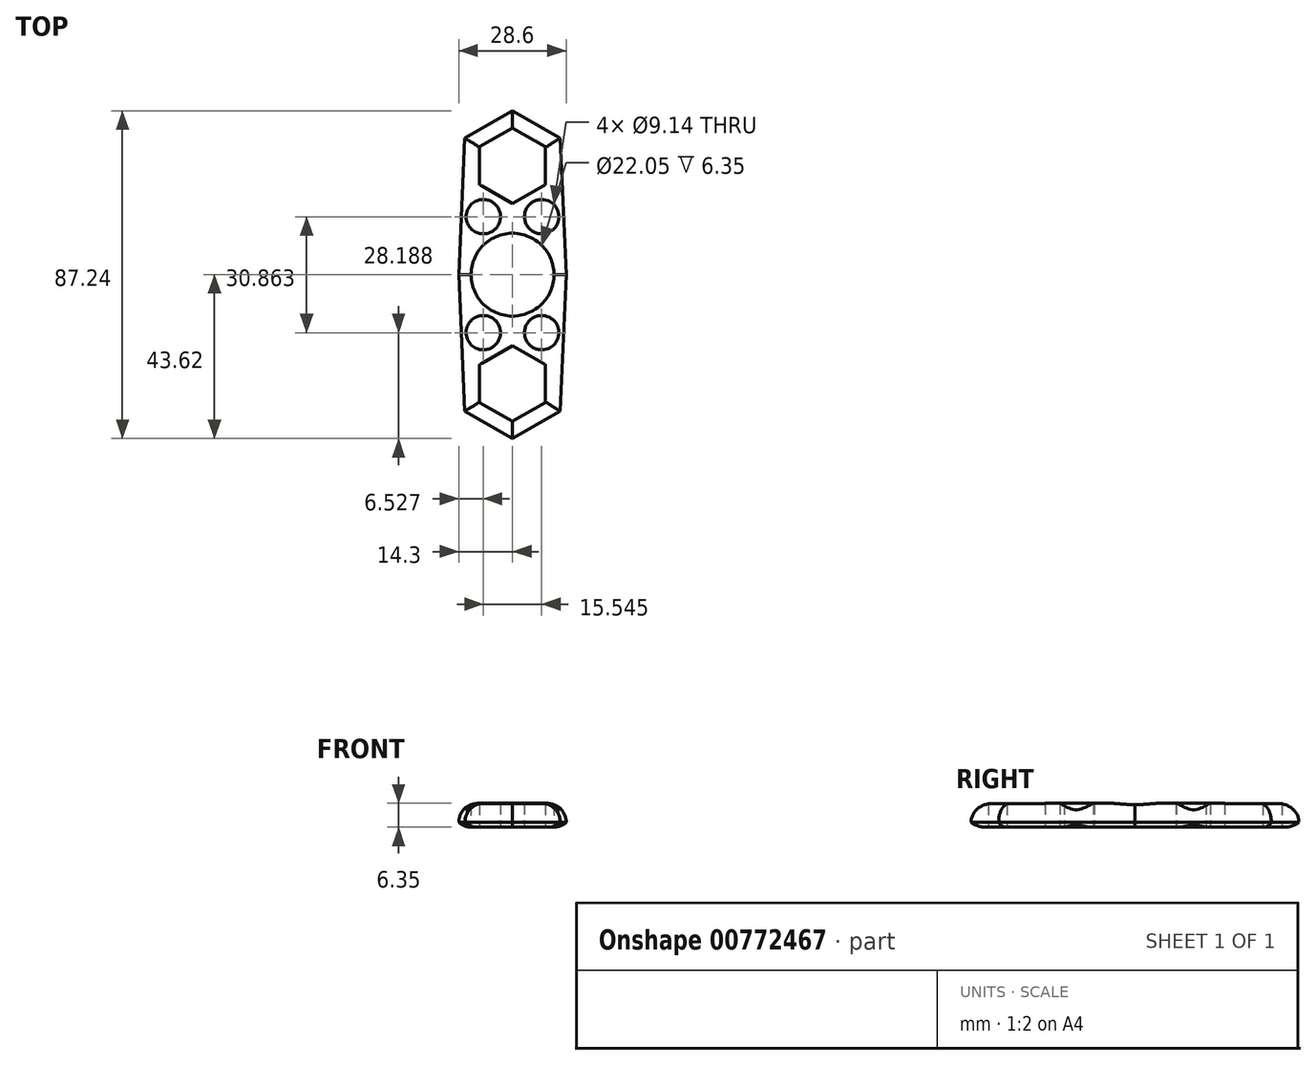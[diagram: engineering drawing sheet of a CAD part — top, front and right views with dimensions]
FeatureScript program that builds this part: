
annotation { "Feature Type Name" : "Feature", "Feature Type Description" : "" }
export const myFeature = defineFeature(function(context is Context, id is Id, definition is map)
    precondition{}
    {
        {
            var Q0;
            Q0=qCreatedBy(makeId("Top.planeOp"),FACE);
            var sketch = newSketch(context, id + "F0", { "sketchPlane" : qUnion([Q0])});
            skCircle(sketch, "E0", {"center": v(0, 0) * mm, "radius": 14.29 * mm});
            skCircle(sketch, "E1", {"center": v(0, 0) * mm, "radius": 11.02 * mm});
            skCircle(sketch, "E2.cCircle", {"center": v(0, 28.95) * mm, "radius": 12.7 * mm, "construction": true});
            skLineSegment(sketch, "E2.0", {"start": v(0, 14.29) * mm, "end": v(-12.7, 21.62) * mm});
            skLineSegment(sketch, "E2.1", {"start": v(-12.7, 21.62) * mm, "end": v(-12.7, 36.28) * mm});
            skLineSegment(sketch, "E2.2", {"start": v(-12.7, 36.28) * mm, "end": v(0, 43.62) * mm});
            skLineSegment(sketch, "E2.3", {"start": v(0, 43.62) * mm, "end": v(12.7, 36.28) * mm});
            skLineSegment(sketch, "E2.4", {"start": v(12.7, 36.28) * mm, "end": v(12.7, 21.62) * mm});
            skLineSegment(sketch, "E2.5", {"start": v(12.7, 21.62) * mm, "end": v(0, 14.29) * mm});
            skPoint(sketch, "E2.0.midPoint", {"position": v(-6.35, 17.95) * mm});
            skCircle(sketch, "E3.cCircle", {"center": v(0, 28.95) * mm, "radius": 8.74 * mm, "construction": true});
            skLineSegment(sketch, "E3.0", {"start": v(-8.74, 23.9) * mm, "end": v(-8.74, 34) * mm});
            skLineSegment(sketch, "E3.1", {"start": v(-8.74, 34) * mm, "end": v(0, 39.04) * mm});
            skLineSegment(sketch, "E3.2", {"start": v(0, 39.04) * mm, "end": v(8.74, 34) * mm});
            skLineSegment(sketch, "E3.3", {"start": v(8.74, 34) * mm, "end": v(8.74, 23.9) * mm});
            skLineSegment(sketch, "E3.4", {"start": v(8.74, 23.9) * mm, "end": v(0, 18.86) * mm});
            skLineSegment(sketch, "E3.5", {"start": v(0, 18.86) * mm, "end": v(-8.74, 23.9) * mm});
            skPoint(sketch, "E3.0.midPoint", {"position": v(-8.74, 28.95) * mm});
            skLineSegment(sketch, "E4.1.0", {"start": v(-8.74, -23.9) * mm, "end": v(0, -18.86) * mm});
            skCircle(sketch, "E4.1.1", {"center": v(0, -28.95) * mm, "radius": 8.74 * mm, "construction": true});
            skLineSegment(sketch, "E4.1.2", {"start": v(-12.7, -21.62) * mm, "end": v(0, -14.29) * mm});
            skLineSegment(sketch, "E4.1.3", {"start": v(-8.74, -34) * mm, "end": v(-8.74, -23.9) * mm});
            skLineSegment(sketch, "E4.1.4", {"start": v(-12.7, -36.28) * mm, "end": v(-12.7, -21.62) * mm});
            skPoint(sketch, "E4.1.5", {"position": v(8.74, -28.95) * mm});
            skCircle(sketch, "E4.1.6", {"center": v(0, -28.95) * mm, "radius": 12.7 * mm, "construction": true});
            skLineSegment(sketch, "E4.1.7", {"start": v(0, -43.62) * mm, "end": v(-12.7, -36.28) * mm});
            skLineSegment(sketch, "E4.1.8", {"start": v(12.7, -36.28) * mm, "end": v(0, -43.62) * mm});
            skPoint(sketch, "E4.1.9", {"position": v(6.35, -17.95) * mm});
            skLineSegment(sketch, "E4.1.10", {"start": v(0, -39.04) * mm, "end": v(-8.74, -34) * mm});
            skLineSegment(sketch, "E4.1.11", {"start": v(12.7, -21.62) * mm, "end": v(12.7, -36.28) * mm});
            skLineSegment(sketch, "E4.1.12", {"start": v(0, -14.29) * mm, "end": v(12.7, -21.62) * mm});
            skLineSegment(sketch, "E4.1.13", {"start": v(8.74, -23.9) * mm, "end": v(8.74, -34) * mm});
            skLineSegment(sketch, "E4.1.14", {"start": v(8.74, -34) * mm, "end": v(0, -39.04) * mm});
            skLineSegment(sketch, "E4.1.15", {"start": v(0, -18.86) * mm, "end": v(8.74, -23.9) * mm});
            skLineSegment(sketch, "E5", {"start": v(-12.7, 36.28) * mm, "end": v(-14.3, 0) * mm});
            skLineSegment(sketch, "E6", {"start": v(-14.3, 0) * mm, "end": v(-12.7, -36.28) * mm});
            skLineSegment(sketch, "E7", {"start": v(12.7, 36.28) * mm, "end": v(14.3, 0) * mm});
            skLineSegment(sketch, "E8", {"start": v(14.3, 0) * mm, "end": v(12.7, -36.28) * mm});
            skCircle(sketch, "E9", {"center": v(-9.43, -15.39) * mm, "radius": 3.18 * mm, "construction": true});
            skCircle(sketch, "E10.MirrorC", {"center": v(-9.43, 15.39) * mm, "radius": 3.18 * mm, "construction": true});
            skCircle(sketch, "E11.MirrorC", {"center": v(9.43, -15.39) * mm, "radius": 3.18 * mm, "construction": true});
            skCircle(sketch, "E12.MirrorC", {"center": v(9.43, 15.39) * mm, "radius": 3.18 * mm, "construction": true});
            skSolve(sketch);
        }
        {
            var Q0;
            {var subQ0=sQuery(id+"F0.wireOp",EDGE,"E5");var subQ1=sQuery(id+"F0.wireOp",EDGE,"E0");var subQ2=makeQuery(id+"F0.imprint","INTERSECT",VERTEX,{"derivedFrom":[subQ1,subQ0]});Q0=makeQuery(id+"F0.imprint","IMPRINT",FACE,{"disambiguationData":[TD([[makeQuery(id+"F0.imprint","IMPRINT",EDGE,{"disambiguationData":[TD([[subQ2,-1.0]])],"derivedFrom":subQ1}),-1.0]])]});}
            var Q1;
            {var subQ0=sQuery(id+"F0.wireOp",EDGE,"E7");var subQ1=sQuery(id+"F0.wireOp",EDGE,"E0");var subQ2=makeQuery(id+"F0.imprint","INTERSECT",VERTEX,{"derivedFrom":[subQ1,subQ0]});Q1=makeQuery(id+"F0.imprint","IMPRINT",FACE,{"disambiguationData":[TD([[makeQuery(id+"F0.imprint","IMPRINT",EDGE,{"disambiguationData":[TD([[subQ2,1.0]])],"derivedFrom":subQ1}),-1.0]])]});}
            var Q2;
            {var subQ0=sQuery(id+"F0.wireOp",EDGE,"E4.1.2");Q2=makeQuery(id+"F0.imprint","IMPRINT",FACE,{"disambiguationData":[TD([[makeQuery(id+"F0.imprint","IMPRINT",EDGE,{"derivedFrom":subQ0}),1.0]])]});}
            var Q3;
            {var subQ4=sQuery(id+"F0.wireOp",EDGE,"E4.1.11");Q3=makeQuery(id+"F0.imprint","IMPRINT",FACE,{"disambiguationData":[TD([[makeQuery(id+"F0.imprint","IMPRINT",EDGE,{"derivedFrom":subQ4}),1.0]])]});}
            var Q4;
            Q4=makeQuery(id+"F0.imprint","IMPRINT",FACE,{"disambiguationData":[TD([[makeQuery(id+"F0.imprint","IMPRINT",EDGE,{"derivedFrom":sQuery(id+"F0.wireOp",EDGE,"E2.0")}),-1.0]])]});
            var Q5;
            Q5=makeQuery(id+"F0.imprint","IMPRINT",FACE,{"disambiguationData":[TD([[makeQuery(id+"F0.imprint","IMPRINT",EDGE,{"derivedFrom":sQuery(id+"F0.wireOp",EDGE,"E4.1.0")}),1.0]])]});
            var Q6;
            Q6=makeQuery(id+"F0.imprint","IMPRINT",FACE,{"disambiguationData":[TD([[makeQuery(id+"F0.imprint","IMPRINT",EDGE,{"derivedFrom":sQuery(id+"F0.wireOp",EDGE,"E1")}),-1.0]])]});
            var Q7;
            {var subQ0=sQuery(id+"F0.wireOp",EDGE,"E2.0");Q7=makeQuery(id+"F0.imprint","IMPRINT",FACE,{"disambiguationData":[TD([[makeQuery(id+"F0.imprint","IMPRINT",EDGE,{"derivedFrom":subQ0}),1.0]])]});}
            var Q8;
            {var subQ4=sQuery(id+"F0.wireOp",EDGE,"E2.4");Q8=makeQuery(id+"F0.imprint","IMPRINT",FACE,{"disambiguationData":[TD([[makeQuery(id+"F0.imprint","IMPRINT",EDGE,{"derivedFrom":subQ4}),1.0]])]});}
            extrude(context, id + "F1", {"entities" : qUnion([Q0, Q1, Q2, Q3, Q4, Q5, Q6, Q7, Q8]), "depth" : 6.35 * mm, "offsetDistance" : 25.4 * mm});
        }
        {
            var Q0;
            Q0=qCreatedBy(makeId("Top.planeOp"),FACE);
            var sketch = newSketch(context, id + "F2", { "sketchPlane" : qUnion([Q0])});
            skCircle(sketch, "E13", {"center": v(-7.77, 15.43) * mm, "radius": 4.57 * mm});
            skCircle(sketch, "E14.MirrorC", {"center": v(7.77, 15.43) * mm, "radius": 4.57 * mm});
            skCircle(sketch, "E15.MirrorC", {"center": v(-7.77, -15.43) * mm, "radius": 4.57 * mm});
            skCircle(sketch, "E16.MirrorC", {"center": v(7.77, -15.43) * mm, "radius": 4.57 * mm});
            skSolve(sketch);
        }
        {
            var Q0;
            Q0 = qSketchRegion(id + "F2", true);
            extrude(context, id + "F3", {"entities" : qUnion([Q0]), "operationType" : NewBodyOperationType.REMOVE, "endBound" : BoundingType.THROUGH_ALL, "depth" : 25.4 * mm, "offsetDistance" : 25.4 * mm});
        }
        {
            var Q0;
            Q0=makeQuery(id+"F1.opExtrude","CAP_EDGE",EDGE,{"disambiguationData":[OSD([sQuery(id+"F0.wireOp",EDGE,"E2.2")])],"isStart":false});
            var Q1;
            Q1=makeQuery(id+"F1.opExtrude","CAP_EDGE",EDGE,{"disambiguationData":[OSD([sQuery(id+"F0.wireOp",EDGE,"E2.3")])],"isStart":false});
            var Q2;
            Q2=makeQuery(id+"F1.opExtrude","CAP_EDGE",EDGE,{"disambiguationData":[OSD([sQuery(id+"F0.wireOp",EDGE,"E7")])],"isStart":false});
            var Q3;
            Q3=makeQuery(id+"F1.opExtrude","CAP_EDGE",EDGE,{"disambiguationData":[OSD([sQuery(id+"F0.wireOp",EDGE,"E8")])],"isStart":false});
            var Q4;
            Q4=makeQuery(id+"F1.opExtrude","CAP_EDGE",EDGE,{"disambiguationData":[OSD([sQuery(id+"F0.wireOp",EDGE,"E4.1.8")])],"isStart":false});
            var Q5;
            Q5=makeQuery(id+"F1.opExtrude","CAP_EDGE",EDGE,{"disambiguationData":[OSD([sQuery(id+"F0.wireOp",EDGE,"E4.1.7")])],"isStart":false});
            var Q6;
            Q6=makeQuery(id+"F1.opExtrude","CAP_EDGE",EDGE,{"disambiguationData":[OSD([sQuery(id+"F0.wireOp",EDGE,"E6")])],"isStart":false});
            var Q7;
            Q7=makeQuery(id+"F1.opExtrude","CAP_EDGE",EDGE,{"disambiguationData":[OSD([sQuery(id+"F0.wireOp",EDGE,"E5")])],"isStart":false});
            fillet(context, id + "F4", {"entities" : qUnion([Q0, Q1, Q2, Q3, Q4, Q5, Q6, Q7]), "radius" : 5.08 * mm, "tangentPropagation" : true, "allowEdgeOverflow" : false});
        }
        {
            var Q0;
            Q0=makeQuery(id+"F1.opExtrude","CAP_EDGE",EDGE,{"disambiguationData":[OSD([sQuery(id+"F0.wireOp",EDGE,"E7")])],"isStart":true});
            var Q1;
            Q1=makeQuery(id+"F1.opExtrude","CAP_EDGE",EDGE,{"disambiguationData":[OSD([sQuery(id+"F0.wireOp",EDGE,"E2.3")])],"isStart":true});
            var Q2;
            Q2=makeQuery(id+"F1.opExtrude","CAP_EDGE",EDGE,{"disambiguationData":[OSD([sQuery(id+"F0.wireOp",EDGE,"E2.2")])],"isStart":true});
            var Q3;
            Q3=makeQuery(id+"F1.opExtrude","CAP_EDGE",EDGE,{"disambiguationData":[OSD([sQuery(id+"F0.wireOp",EDGE,"E5")])],"isStart":true});
            var Q4;
            Q4=makeQuery(id+"F1.opExtrude","CAP_EDGE",EDGE,{"disambiguationData":[OSD([sQuery(id+"F0.wireOp",EDGE,"E6")])],"isStart":true});
            var Q5;
            Q5=makeQuery(id+"F1.opExtrude","CAP_EDGE",EDGE,{"disambiguationData":[OSD([sQuery(id+"F0.wireOp",EDGE,"E4.1.7")])],"isStart":true});
            var Q6;
            Q6=makeQuery(id+"F1.opExtrude","CAP_EDGE",EDGE,{"disambiguationData":[OSD([sQuery(id+"F0.wireOp",EDGE,"E4.1.8")])],"isStart":true});
            var Q7;
            Q7=makeQuery(id+"F1.opExtrude","CAP_EDGE",EDGE,{"disambiguationData":[OSD([sQuery(id+"F0.wireOp",EDGE,"E8")])],"isStart":true});
            fillet(context, id + "F5", {"entities" : qUnion([Q0, Q1, Q2, Q3, Q4, Q5, Q6, Q7]), "radius" : 5.08 * mm, "tangentPropagation" : true, "allowEdgeOverflow" : false});
        }
    });
